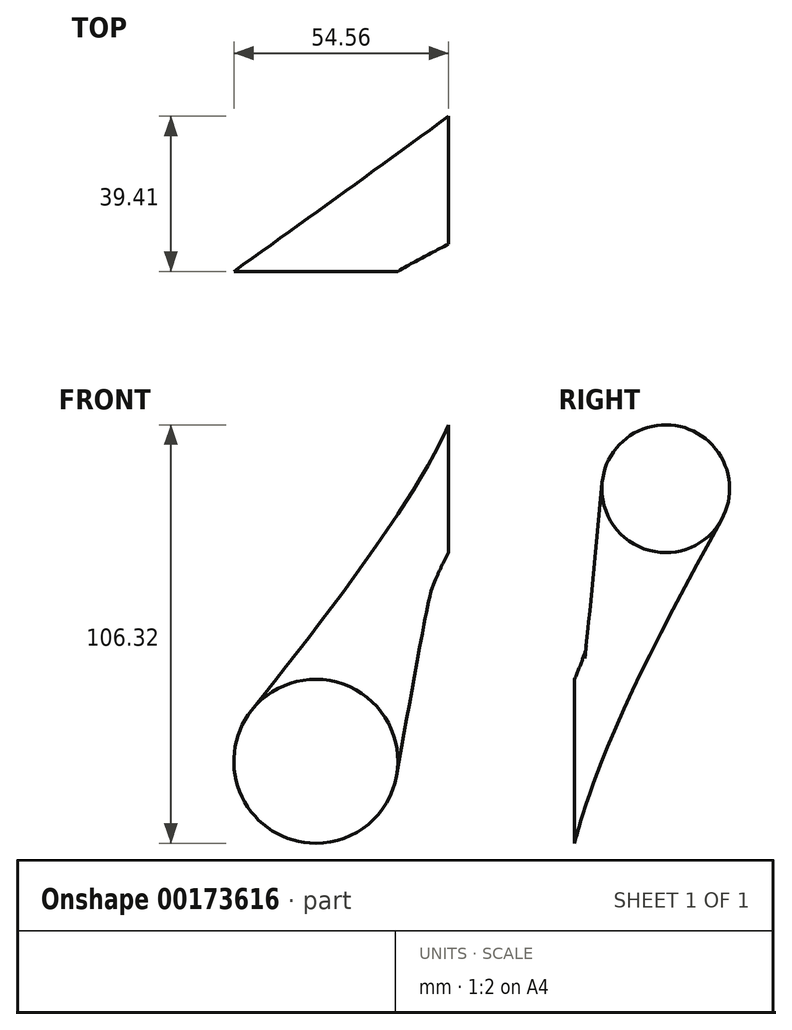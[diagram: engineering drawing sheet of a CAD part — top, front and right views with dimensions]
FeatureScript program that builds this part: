
annotation { "Feature Type Name" : "Feature", "Feature Type Description" : "" }
export const myFeature = defineFeature(function(context is Context, id is Id, definition is map)
    precondition{}
    {
        {
            var Q0;
            Q0=qCreatedBy(makeId("Front.planeOp"),FACE);
            var sketch = newSketch(context, id + "F0", { "sketchPlane" : qUnion([Q0])});
            skCircle(sketch, "E0", {"center": v(-33.73, -42.67) * mm, "radius": 20.83 * mm});
            skSolve(sketch);
        }
        {
            var Q0;
            Q0=qCreatedBy(makeId("Right.planeOp"),FACE);
            var sketch = newSketch(context, id + "F1", { "sketchPlane" : qUnion([Q0])});
            skCircle(sketch, "E1", {"center": v(23.17, 26.58) * mm, "radius": 16.24 * mm});
            skSolve(sketch);
        }
        {
            var Q0;
            Q0=makeQuery(id+"F0.imprint","IMPRINT",FACE,{"disambiguationData":[TD([[makeQuery(id+"F0.imprint","IMPRINT",EDGE,{"derivedFrom":sQuery(id+"F0.wireOp",EDGE,"E0")}),1.0]])]});
            var Q1;
            Q1=makeQuery(id+"F1.imprint","IMPRINT",FACE,{"disambiguationData":[TD([[makeQuery(id+"F1.imprint","IMPRINT",EDGE,{"derivedFrom":sQuery(id+"F1.wireOp",EDGE,"E1")}),1.0]])]});
            loft(context, id + "F2", {"sheetProfilesArray" : [{ "sheetProfileEntities" : qUnion([Q0]) }, { "sheetProfileEntities" : qUnion([Q1]) }]});
        }
    });
